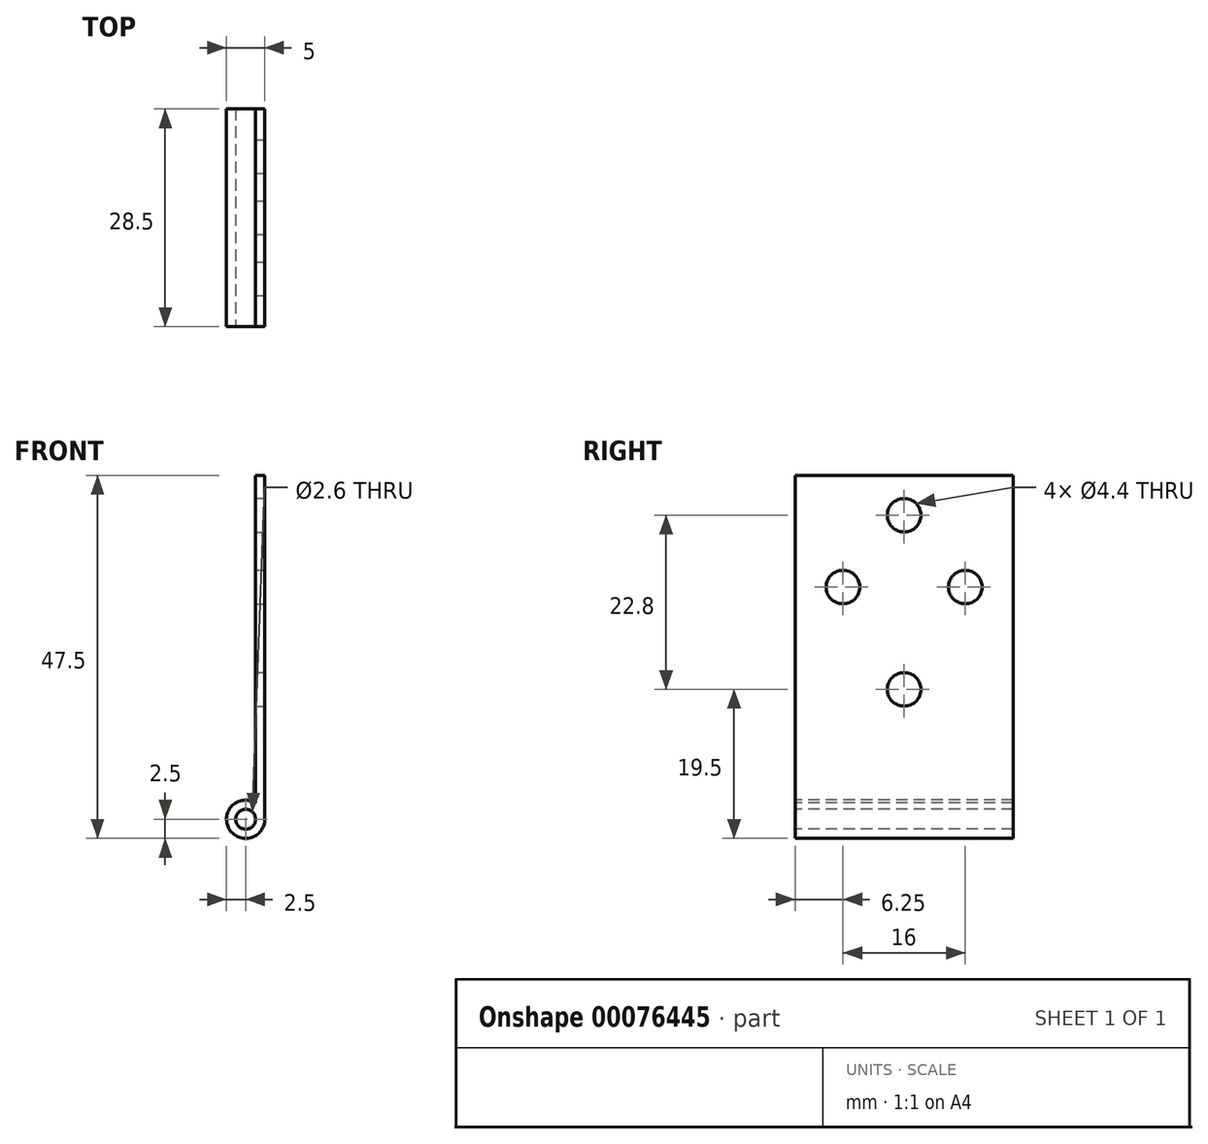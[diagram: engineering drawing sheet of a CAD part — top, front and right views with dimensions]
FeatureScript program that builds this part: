
annotation { "Feature Type Name" : "Feature", "Feature Type Description" : "" }
export const myFeature = defineFeature(function(context is Context, id is Id, definition is map)
    precondition{}
    {
        {
            var Q0;
            Q0=qCreatedBy(makeId("Front.planeOp"),FACE);
            var sketch = newSketch(context, id + "F0", { "sketchPlane" : qUnion([Q0])});
            skCircle(sketch, "E0", {"center": v(0, 0) * mm, "radius": 2.5 * mm});
            skLineSegment(sketch, "E1", {"start": v(2.5, 0) * mm, "end": v(2.5, 45) * mm});
            skLineSegment(sketch, "E2.0", {"start": v(1.3, 0) * mm, "end": v(1.3, 45) * mm});
            skLineSegment(sketch, "E3", {"start": v(1.3, 45) * mm, "end": v(2.5, 45) * mm});
            skSolve(sketch);
        }
        {
            var Q0;
            {var subQ0=sQuery(id+"F0.wireOp",EDGE,"E1");Q0=makeQuery(id+"F0.imprint","IMPRINT",FACE,{"disambiguationData":[TD([[makeQuery(id+"F0.imprint","IMPRINT",EDGE,{"derivedFrom":subQ0}),1.0]])]});}
            var Q1;
            {var subQ0=sQuery(id+"F0.wireOp",EDGE,"E0");var subQ1=makeQuery(id+"F0.imprint","INTERSECT",VERTEX,{"derivedFrom":[subQ0,sQuery(id+"F0.wireOp",EDGE,"E1")]});Q1=makeQuery(id+"F0.imprint","IMPRINT",FACE,{"disambiguationData":[TD([[makeQuery(id+"F0.imprint","IMPRINT",EDGE,{"disambiguationData":[TD([[subQ1,-1.0]])],"derivedFrom":subQ0}),1.0]])]});}
            extrude(context, id + "F1", {"entities" : qUnion([Q0, Q1]), "oppositeDirection" : true, "depth" : 28.5 * mm});
        }
        {
            var Q0;
            Q0=sQuery(id+"F0.wireOp",VERTEX,"E0.center");
            var Q1;
            Q1=makeQuery(id+"F1.opExtrude","SWEPT_BODY",BODY,{"disambiguationData":[OSD([sQuery(id+"F0.wireOp",EDGE,"E0"),sQuery(id+"F0.wireOp",EDGE,"E1"),sQuery(id+"F0.wireOp",EDGE,"E2.0"),sQuery(id+"F0.wireOp",EDGE,"E3")])]});
            hole(context, id + "F2", {"style" : HoleStyle.SIMPLE, "endStyle" : HoleEndStyle.THROUGH, "standardTappedOrClearance" : lookupTablePath({ "standard" : "ISO", "size" : "2.6", "type" : "Drilled" }), "standardBlindInLast" : lookupTablePath({ "standard" : "ISO", "size" : "2.6", "type" : "Drilled" }), "holeDiameter" : 2.6 * mm, "startFromSketch" : true, "locations" : qUnion([Q0]), "scope" : qUnion([Q1]), "isTappedThrough" : true});
        }
        {
            var Q0;
            Q0=makeQuery(id+"F1.opExtrude","SWEPT_FACE",FACE,{"disambiguationData":[OSD([sQuery(id+"F0.wireOp",EDGE,"E1")])]});
            var sketch = newSketch(context, id + "F3", { "sketchPlane" : qUnion([Q0])});
            skLineSegment(sketch, "E4", {"start": v(14.25, 45) * mm, "end": v(14.25, 0) * mm, "construction": true});
            skLineSegment(sketch, "E5", {"start": v(28.5, 30.4) * mm, "end": v(0, 30.4) * mm, "construction": true});
            skPoint(sketch, "E6", {"position": v(14.25, 39.8) * mm});
            skPoint(sketch, "E7", {"position": v(22.25, 30.4) * mm});
            skPoint(sketch, "E8", {"position": v(6.25, 30.4) * mm});
            skPoint(sketch, "E9", {"position": v(14.25, 17) * mm});
            skSolve(sketch);
        }
        {
            var Q0;
            Q0=sQuery(id+"F3.wireOp",VERTEX,"E6");
            var Q1;
            Q1=sQuery(id+"F3.wireOp",VERTEX,"E7");
            var Q2;
            Q2=sQuery(id+"F3.wireOp",VERTEX,"E8");
            var Q3;
            Q3=sQuery(id+"F3.wireOp",VERTEX,"E9");
            var Q4;
            Q4=makeQuery(id+"F1.opExtrude","SWEPT_BODY",BODY,{"disambiguationData":[OSD([sQuery(id+"F0.wireOp",EDGE,"E0"),sQuery(id+"F0.wireOp",EDGE,"E1"),sQuery(id+"F0.wireOp",EDGE,"E2.0"),sQuery(id+"F0.wireOp",EDGE,"E3")])]});
            hole(context, id + "F4", {"style" : HoleStyle.SIMPLE, "endStyle" : HoleEndStyle.THROUGH, "standardTappedOrClearance" : lookupTablePath({ "standard" : "ISO", "size" : "4.4", "type" : "Drilled" }), "standardBlindInLast" : lookupTablePath({ "standard" : "ISO", "size" : "4.4", "type" : "Drilled" }), "holeDiameter" : 4.4 * mm, "startFromSketch" : true, "locations" : qUnion([Q0, Q1, Q2, Q3]), "scope" : qUnion([Q4]), "isTappedThrough" : true});
        }
    });
